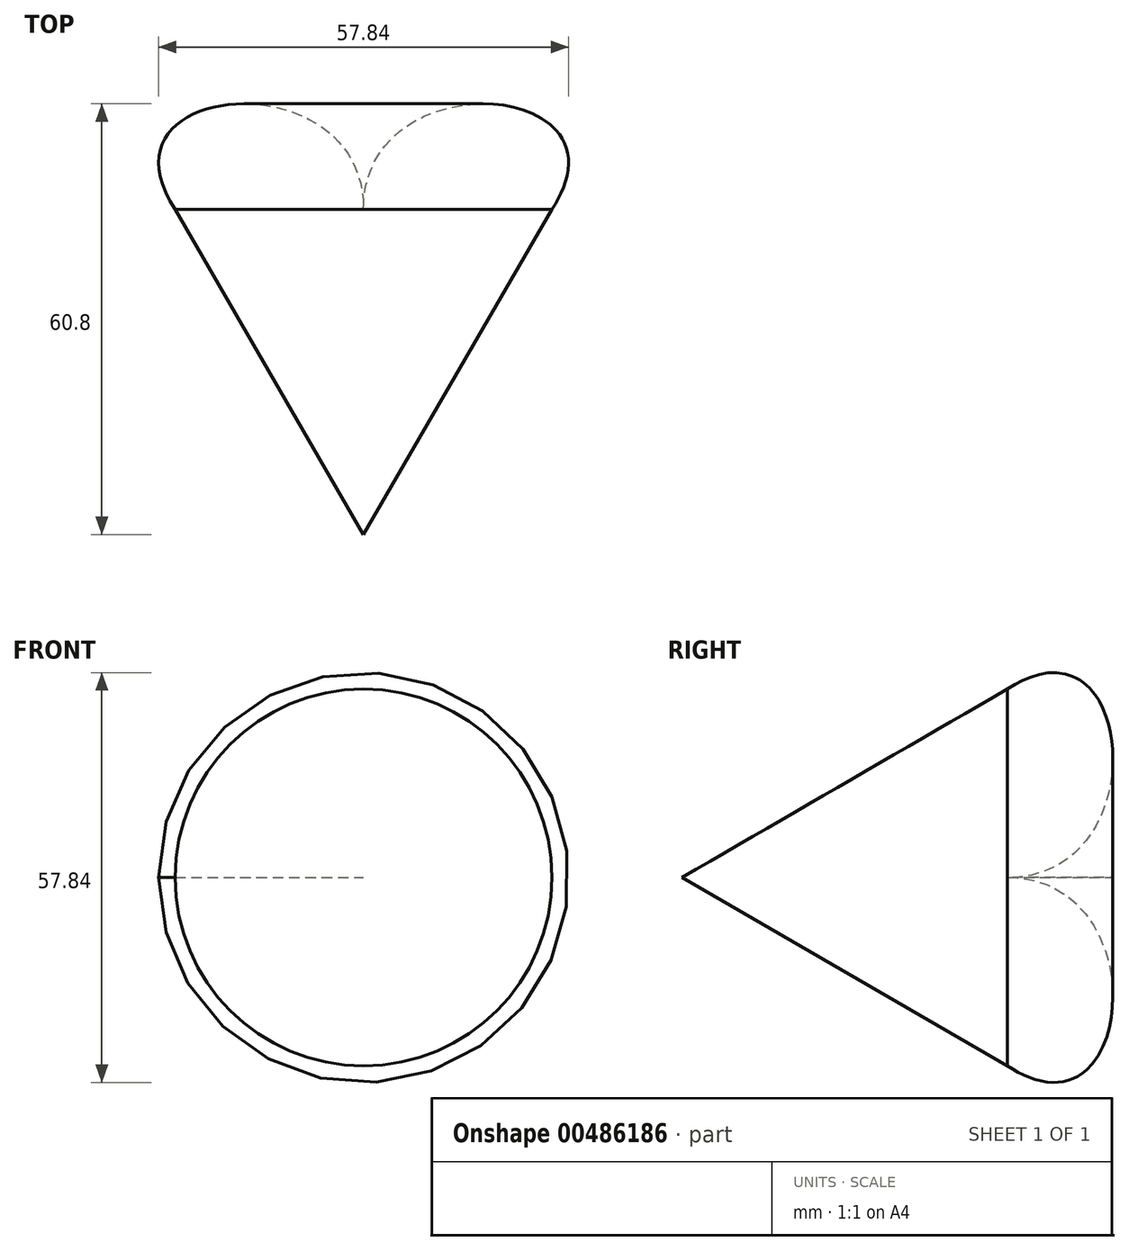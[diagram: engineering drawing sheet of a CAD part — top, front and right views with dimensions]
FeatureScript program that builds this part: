
annotation { "Feature Type Name" : "Feature", "Feature Type Description" : "" }
export const myFeature = defineFeature(function(context is Context, id is Id, definition is map)
    precondition{}
    {
        {
            var Q0;
            Q0=qCreatedBy(makeId("Top.planeOp"),FACE);
            var sketch = newSketch(context, id + "F0", { "sketchPlane" : qUnion([Q0])});
            skFitSpline(sketch, "E0", {"points": [v(-26.6, 0) * mm, v(0, 0) * mm], "startDerivative": vector(-36.13, 54.94) * mm, "endDerivative": vector(0, -63.98) * mm});
            skLineSegment(sketch, "E1", {"start": v(-26.6, 0) * mm, "end": v(0, -45.91) * mm});
            skLineSegment(sketch, "E2", {"start": v(0, 0) * mm, "end": v(0, -45.91) * mm});
            skSolve(sketch);
        }
        {
            var Q0;
            Q0 = qSketchRegion(id + "F0", true);
            var Q1;
            Q1=sQuery(id+"F0.wireOp",EDGE,"E2");
            revolve(context, id + "F1", {"entities" : qUnion([Q0]), "axis" : qUnion([Q1]), "revolveType" : RevolveType.FULL});
        }
    });
